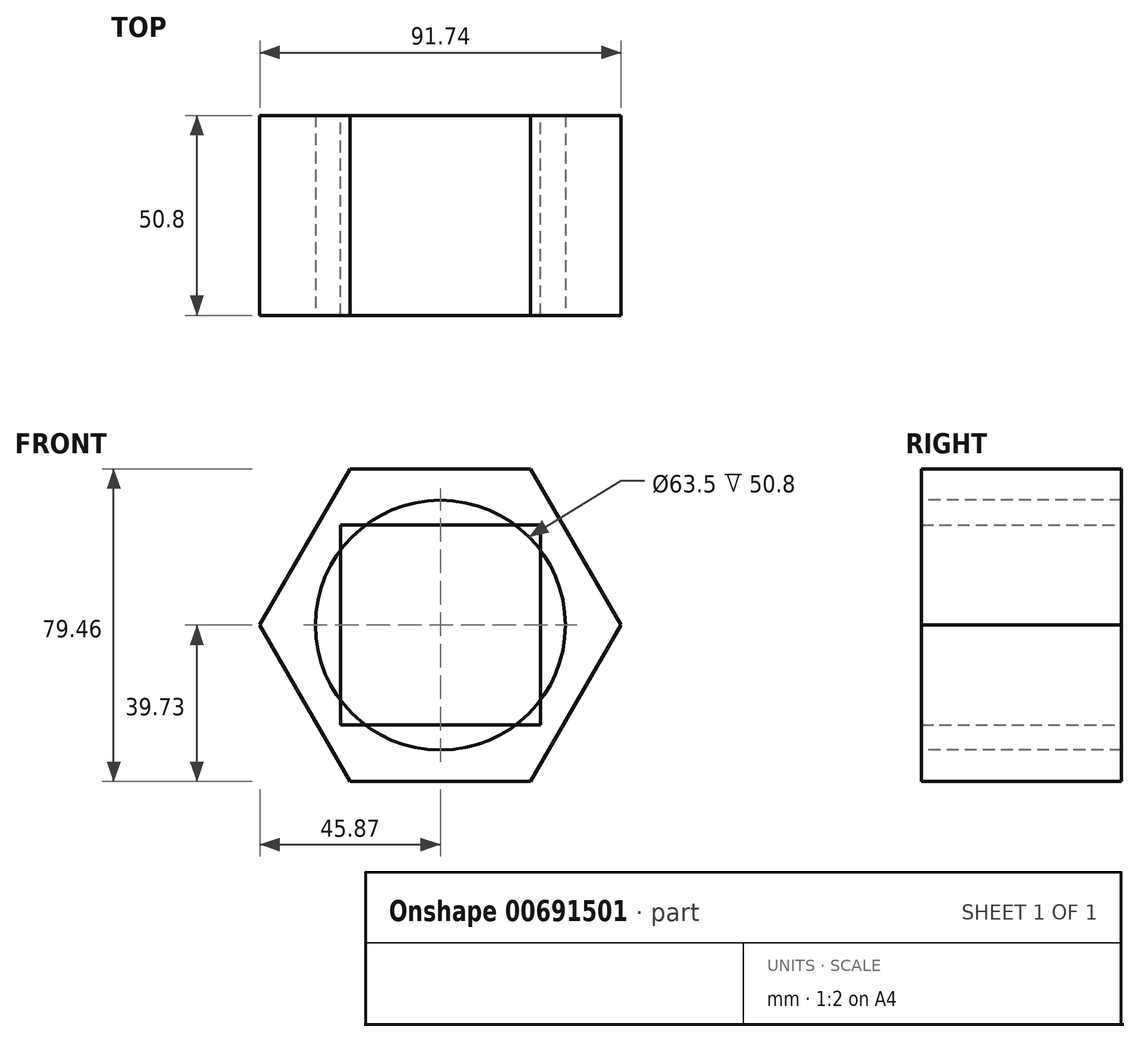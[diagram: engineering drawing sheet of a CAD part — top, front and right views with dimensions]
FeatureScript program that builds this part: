
annotation { "Feature Type Name" : "Feature", "Feature Type Description" : "" }
export const myFeature = defineFeature(function(context is Context, id is Id, definition is map)
    precondition{}
    {
        {
            var Q0;
            Q0=qCreatedBy(makeId("Front.planeOp"),FACE);
            var sketch = newSketch(context, id + "F0", { "sketchPlane" : qUnion([Q0])});
            skCircle(sketch, "E0.cCircle", {"center": v(0, 0) * mm, "radius": 39.73 * mm, "construction": true});
            skLineSegment(sketch, "E0.0", {"start": v(-22.94, 39.73) * mm, "end": v(22.94, 39.73) * mm});
            skLineSegment(sketch, "E0.1", {"start": v(22.94, 39.73) * mm, "end": v(45.87, 0) * mm});
            skLineSegment(sketch, "E0.2", {"start": v(45.87, 0) * mm, "end": v(22.94, -39.73) * mm});
            skLineSegment(sketch, "E0.3", {"start": v(22.94, -39.73) * mm, "end": v(-22.94, -39.73) * mm});
            skLineSegment(sketch, "E0.4", {"start": v(-22.94, -39.73) * mm, "end": v(-45.87, 0) * mm});
            skLineSegment(sketch, "E0.5", {"start": v(-45.87, 0) * mm, "end": v(-22.94, 39.73) * mm});
            skPoint(sketch, "E0.0.midPoint", {"position": v(0, 39.73) * mm});
            skSolve(sketch);
        }
        {
            var Q0;
            Q0=qCreatedBy(makeId("Front.planeOp"),FACE);
            var sketch = newSketch(context, id + "F1", { "sketchPlane" : qUnion([Q0])});
            skLineSegment(sketch, "E1.bottom", {"start": v(25.4, 25.4) * mm, "end": v(-25.4, 25.4) * mm});
            skLineSegment(sketch, "E1.top", {"start": v(25.4, -25.4) * mm, "end": v(-25.4, -25.4) * mm});
            skLineSegment(sketch, "E1.left", {"start": v(25.4, 25.4) * mm, "end": v(25.4, -25.4) * mm});
            skLineSegment(sketch, "E1.right", {"start": v(-25.4, 25.4) * mm, "end": v(-25.4, -25.4) * mm});
            skPoint(sketch, "E1.middle", {"position": v(0, 0) * mm});
            skSolve(sketch);
        }
        {
            var Q0;
            Q0 = qSketchRegion(id + "F0", true);
            extrude(context, id + "F2", {"entities" : qUnion([Q0]), "endBound" : BoundingType.SYMMETRIC, "depth" : 50.8 * mm, "offsetDistance" : 25.4 * mm});
        }
        {
            var Q0;
            Q0=makeQuery(id+"F1.imprint","IMPRINT",FACE,{"disambiguationData":[TD([[makeQuery(id+"F1.imprint","IMPRINT",EDGE,{"derivedFrom":sQuery(id+"F1.wireOp",EDGE,"E1.bottom")}),1.0]])]});
            extrude(context, id + "F3", {"entities" : qUnion([Q0]), "endBound" : BoundingType.SYMMETRIC, "depth" : 50.8 * mm, "offsetDistance" : 25.4 * mm});
        }
        {
            var Q0;
            Q0=sQuery(id+"F1.wireOp",VERTEX,"E1.middle");
            var Q1;
            Q1=makeQuery(id+"F2.opExtrude","SWEPT_BODY",BODY,{"disambiguationData":[OSD([sQuery(id+"F0.wireOp",EDGE,"E0.0"),sQuery(id+"F0.wireOp",EDGE,"E0.1"),sQuery(id+"F0.wireOp",EDGE,"E0.2"),sQuery(id+"F0.wireOp",EDGE,"E0.3"),sQuery(id+"F0.wireOp",EDGE,"E0.4"),sQuery(id+"F0.wireOp",EDGE,"E0.5")])]});
            hole(context, id + "F4", {"style" : HoleStyle.SIMPLE, "endStyle" : HoleEndStyle.THROUGH, "holeDiameter" : 63.5 * mm, "majorDiameter" : 6.35 * mm, "isTappedThrough" : true, "tappedDepth" : 12.7 * mm, "tapClearance" : 3, "locations" : qUnion([Q0]), "scope" : qUnion([Q1])});
        }
        {
            var Q0;
            Q0=sQuery(id+"F0.wireOp",VERTEX,"E0.cCircle.center");
            var Q1;
            Q1=makeQuery(id+"F2.opExtrude","SWEPT_BODY",BODY,{"disambiguationData":[OSD([sQuery(id+"F0.wireOp",EDGE,"E0.0"),sQuery(id+"F0.wireOp",EDGE,"E0.1"),sQuery(id+"F0.wireOp",EDGE,"E0.2"),sQuery(id+"F0.wireOp",EDGE,"E0.3"),sQuery(id+"F0.wireOp",EDGE,"E0.4"),sQuery(id+"F0.wireOp",EDGE,"E0.5")])]});
            hole(context, id + "F5", {"style" : HoleStyle.SIMPLE, "endStyle" : HoleEndStyle.THROUGH, "oppositeDirection" : true, "holeDiameter" : 63.5 * mm, "majorDiameter" : 6.35 * mm, "isTappedThrough" : true, "tappedDepth" : 12.7 * mm, "tapClearance" : 3, "locations" : qUnion([Q0]), "scope" : qUnion([Q1])});
        }
    });
